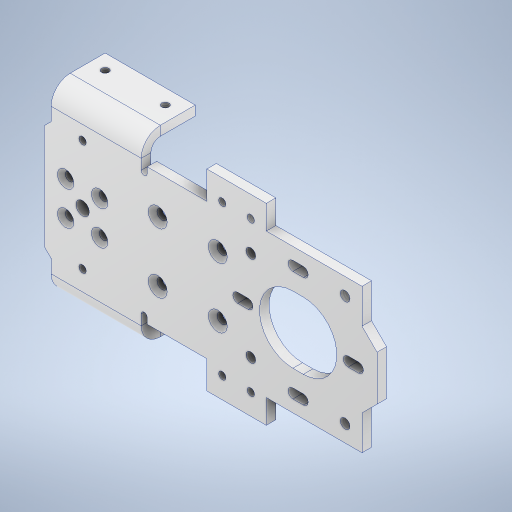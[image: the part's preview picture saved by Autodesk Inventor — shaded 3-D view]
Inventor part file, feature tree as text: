
AUTODESK INVENTOR PART (.ipt)
format: ipt  version: 2024 (Build 280153000, 153)  size: 677,888 bytes
history: native  units: mm
features: sheet_metal_op x17, hole x9, other x8, plane x5, sketch x4, mirror x3, extrude x2, projected_geometry x2
ambient origin geometry x8: Origin, YZ Plane, XZ Plane, XY Plane, X Axis, Y Axis, Z Axis, Center Point
bodies: Solid1 (feature_tree)
feature tree (50):
  sketch  "Sketch1"  dims[d0=27.0mm d1=45.4mm]
  sheet_metal_op  "Face1"
  hole  "Hole1"  [1 undecoded]
  hole  "Hole2"  [1 undecoded]
  hole  "Hole3"  [1 undecoded]
  hole  "Hole4"  [1 undecoded]
  sheet_metal_op  "Face3"
  hole  "Hole5"  [1 undecoded]
  sheet_metal_op  "Face4"
  hole  "Hole6"  [1 undecoded]
  mirror  "Mirror1"
  hole  "Hole7"  [1 undecoded]
  mirror  "Mirror2"
  sketch  "Sketch5"  dims[d2=37.0mm d3=19.5mm]
  sheet_metal_op  "Face5"
  extrude  "Extrusion1"  Depth=6.35mm
  plane  "Work Plane1"
  sheet_metal_op  "Flange1"
  plane  "Work Plane2"
  sheet_metal_op  "Face6"
  hole  "Hole8"  [1 undecoded]
  mirror  "Mirror4"
  sheet_metal_op  "Face7"
  sheet_metal_op  "Flange2"
  extrude  "Extrusion2"  Depth=6.35mm
  hole  "Hole9"  [1 undecoded]
  plane  "Work Plane3"
  plane  "Work Plane5"
  other  "Plate1"
  other  "Plate3"
  sheet_metal_op  "Bend2"
  other  "Plate4"
  sheet_metal_op  "Bend3"
  other  "Plate5"
  sheet_metal_op  "Bend4"
  sketch  "Sketch6"  dims[d4=16.0mm d5=35.0mm]
  other  "Plate6"
  sheet_metal_op  "Bend5"
  sheet_metal_op  "Corner1"
  projected_geometry  "Projected Loop1"
  other  "Plate7"
  sheet_metal_op  "Bend6"
  other  "Plate8"
  sheet_metal_op  "Bend7"
  sketch  "Sketch9"  dims[d6=12.75mm d7=3.175mm d8=20.0mm d9=20.0mm d10=3.4mm d11=8.0mm d12=6.3mm d13=2.0mm d14=90.0deg d15=3.175mm d16=20.594885mm d17=2.9mm d18=8.0mm d19=5.5mm d20=2.0mm d21=90.0deg d22=3.175mm d23=20.594885mm d24=2.459mm d25=6.0mm d26=5.5mm d27=2.0mm d28=90.0deg d29=3.175mm d30=20.594885mm d31=4.5mm d32=6.0mm d33=5.5mm d34=2.0mm d35=90.0deg d36=3.175mm d37=20.594885mm d50=26.0mm d51=1.6mm d52=22.25mm d53=3.5mm d55=22.0mm d56=100.0mm d57=30.0mm d58=10.0mm d59=13.0mm d60=13.0mm d61=4.0mm d62=4.0mm d63=35.2mm d64=14.0mm d65=12.22mm d66=0.63mm d67=37.0mm d68=15.0mm d69=135.0deg d70=8.5mm d76=5.0mm d78=3.175mm d79=3.175mm d80=1.5875mm d81=6.35mm d82=3.175mm d83=3.242mm d84=8.0mm d85=5.5mm d86=2.0mm d87=90.0deg d88=11.8mm d89=20.594885mm d92=19.8mm d93=10.0mm d94=9.5mm d95=3.4mm d96=7.0mm d97=32.0mm d98=3.175mm d99=3.175mm d100=1.5875mm d101=6.35mm d102=3.175mm d103=2.459mm d104=6.0mm d105=5.5mm d106=2.0mm d107=90.0deg d108=8.8mm d109=20.594885mm d110=5.615224mm d111=5.615224mm d112=3.242mm d113=8.0mm d114=5.5mm d115=2.0mm d116=90.0deg d117=11.8mm d118=20.594885mm d119=23.0mm d120=48.0mm d121=7.0mm d122=35.0mm d124=7.0mm d125=4.5mm d126=3.175mm d127=3.175mm d128=1.5875mm d129=6.35mm d130=3.175mm d131=27.0mm d132=3.175mm d133=1.5875mm d134=6.35mm d135=3.175mm d136=10.0mm d137=90.0deg d138=3.175mm d139=12.7mm d140=3.175mm d141=3.175mm d142=2.25mm d143=30.0mm d144=2.0mm d147=45.0deg d148=3.0mm d149=0.0mm d150=0.0mm d151=1.0mm d152=-18.0mm d154=5.0mm d155=3.175mm d156=3.175mm d157=1.5875mm d158=6.35mm d159=3.175mm d160=2.459mm d161=6.0mm d162=5.5mm d163=2.0mm d164=90.0deg d165=8.8mm d166=20.594885mm d167=5.0mm d168=8.5mm d169=30.0deg d170=3.175mm d171=3.175mm d172=1.5875mm d173=6.35mm d174=3.175mm d175=3.175mm d176=1.5875mm d177=6.35mm d178=3.175mm d179=25.0mm d180=90.0deg d181=3.175mm d182=12.7mm d183=3.175mm d184=3.175mm d185=15.0mm d186=120.0deg d187=10.0mm d188=0.0mm d189=8.2mm d190=6.0mm d191=5.5mm d192=2.0mm d193=90.0deg d194=8.8mm d195=20.594885mm d196=13.0mm d197=6.35mm]
  other  "Plate9"
  sheet_metal_op  "Bend8"
  sheet_metal_op  "Corner2"
  projected_geometry  "Projected Loop2"
  plane  "Work Plane4"
note: 9 required parameter values undecoded (feature->parameter linkage not recoverable at this tier; creation-order binding heuristic only, values carry confidence <= 0.55)
